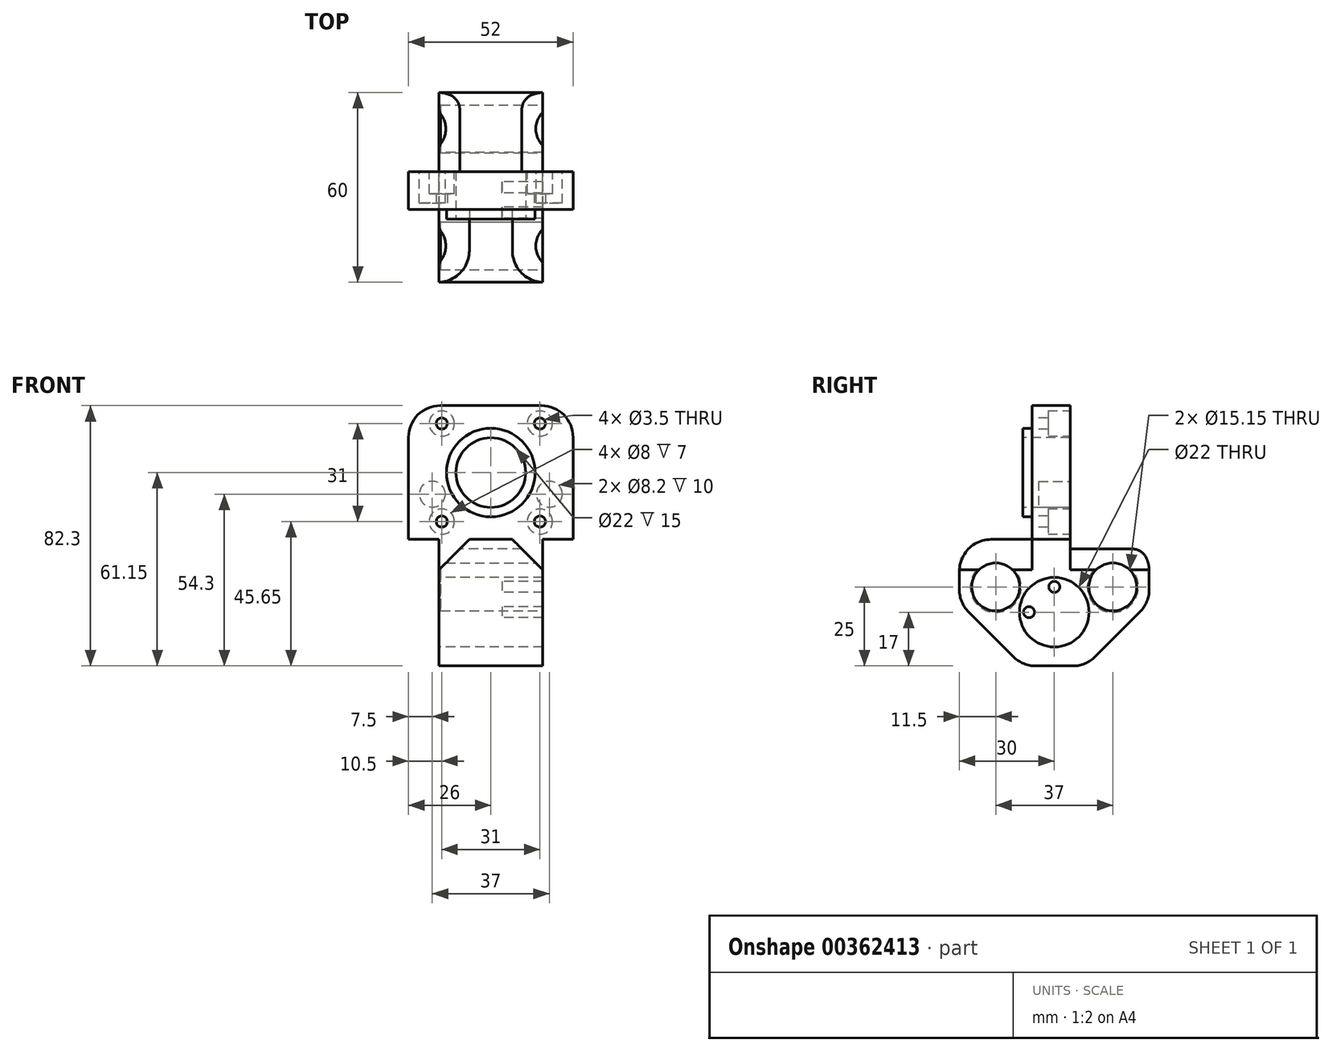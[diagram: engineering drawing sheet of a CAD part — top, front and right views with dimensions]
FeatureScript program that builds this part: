
annotation { "Feature Type Name" : "Feature", "Feature Type Description" : "" }
export const myFeature = defineFeature(function(context is Context, id is Id, definition is map)
    precondition{}
    {
        {
            var Q0;
            Q0=qCreatedBy(makeId("Top.planeOp"),FACE);
            var sketch = newSketch(context, id + "F0", { "sketchPlane" : qUnion([Q0])});
            skLineSegment(sketch, "E0.bottom", {"start": v(16.4, -30) * mm, "end": v(-16.4, -30) * mm});
            skLineSegment(sketch, "E0.top", {"start": v(16.4, 30) * mm, "end": v(-16.4, 30) * mm});
            skLineSegment(sketch, "E0.left", {"start": v(16.4, -30) * mm, "end": v(16.4, 30) * mm});
            skLineSegment(sketch, "E0.right", {"start": v(-16.4, -30) * mm, "end": v(-16.4, 30) * mm});
            skPoint(sketch, "E0.middle", {"position": v(0, 0) * mm});
            skSolve(sketch);
        }
        {
            var Q0;
            Q0=makeQuery(id+"F0.imprint","IMPRINT",FACE,{"disambiguationData":[TD([[makeQuery(id+"F0.imprint","IMPRINT",EDGE,{"derivedFrom":sQuery(id+"F0.wireOp",EDGE,"E0.bottom")}),-1.0]])]});
            extrude(context, id + "F1", {"entities" : qUnion([Q0]), "depth" : 40 * mm});
        }
        {
            var Q0;
            Q0=makeQuery(id+"F1.opExtrude","SWEPT_FACE",FACE,{"disambiguationData":[OSD([sQuery(id+"F0.wireOp",EDGE,"E0.left")])]});
            var sketch = newSketch(context, id + "F2", { "sketchPlane" : qUnion([Q0])});
            skCircle(sketch, "E1", {"center": v(-18.5, 25) * mm, "radius": 7.58 * mm});
            skCircle(sketch, "E2", {"center": v(18.5, 25) * mm, "radius": 7.58 * mm});
            skLineSegment(sketch, "E3", {"start": v(0, 40) * mm, "end": v(0, 0) * mm});
            skCircle(sketch, "E4", {"center": v(0, 17) * mm, "radius": 5.4 * mm});
            skSolve(sketch);
        }
        {
            var Q0;
            Q0=qSketchRegion(id+"F2",true);
            extrude(context, id + "F3", {"entities" : qUnion([Q0]), "operationType" : NewBodyOperationType.REMOVE, "endBound" : BoundingType.THROUGH_ALL, "oppositeDirection" : true, "depth" : 25 * mm});
        }
        {
            var Q0;
            Q0=makeQuery(id+"F1.opExtrude","SWEPT_FACE",FACE,{"disambiguationData":[OSD([sQuery(id+"F0.wireOp",EDGE,"E0.right")])]});
            var sketch = newSketch(context, id + "F4", { "sketchPlane" : qUnion([Q0])});
            skCircle(sketch, "E5", {"center": v(0, 17) * mm, "radius": 11 * mm});
            skSolve(sketch);
        }
        {
            var Q0;
            Q0=makeQuery(id+"F4.imprint","IMPRINT",FACE,{"disambiguationData":[TD([[makeQuery(id+"F4.imprint","IMPRINT",EDGE,{"derivedFrom":sQuery(id+"F4.wireOp",EDGE,"E5")}),1.0]])]});
            extrude(context, id + "F5", {"entities" : qUnion([Q0]), "operationType" : NewBodyOperationType.REMOVE, "oppositeDirection" : true, "depth" : 20 * mm});
        }
        {
            var Q0;
            Q0=makeQuery(id+"F5.boolean.opBoolean","COPY",FACE,{"derivedFrom":makeQuery(id+"F5.opExtrude","CAP_FACE",FACE,{"disambiguationData":[OSD([sQuery(id+"F0.wireOp",EDGE,"E0.right"),sQuery(id+"F2.wireOp",EDGE,"E4"),sQuery(id+"F4.wireOp",EDGE,"E5")])],"isStart":false})});
            var sketch = newSketch(context, id + "F6", { "sketchPlane" : qUnion([Q0])});
            skCircle(sketch, "E6", {"center": v(0, 17) * mm, "radius": 8 * mm});
            skPoint(sketch, "E7", {"position": v(0, 25) * mm});
            skPoint(sketch, "E8", {"position": v(8, 17) * mm});
            skPoint(sketch, "E9", {"position": v(0, 9) * mm});
            skPoint(sketch, "E10", {"position": v(-8, 17) * mm});
            skCircle(sketch, "E11", {"center": v(0, 25) * mm, "radius": 1.75 * mm});
            skCircle(sketch, "E12", {"center": v(8, 17) * mm, "radius": 1.75 * mm});
            skCircle(sketch, "E13", {"center": v(0, 9) * mm, "radius": 1.75 * mm});
            skCircle(sketch, "E14", {"center": v(-8, 17) * mm, "radius": 1.75 * mm});
            skSolve(sketch);
        }
        {
            var Q0;
            {var subQ0=sQuery(id+"F6.wireOp",EDGE,"E11");var subQ1=sQuery(id+"F6.wireOp",EDGE,"E6");var subQ2=makeQuery(id+"F6.imprint","INTERSECT",VERTEX,{"disambiguationData":[OD(0.0)],"derivedFrom":[subQ1,subQ0]});Q0=makeQuery(id+"F6.imprint","IMPRINT",FACE,{"disambiguationData":[TD([[makeQuery(id+"F6.imprint","IMPRINT",EDGE,{"disambiguationData":[TD([[subQ2,-1.0]])],"derivedFrom":subQ1}),1.0]])]});}
            var Q1;
            {var subQ0=sQuery(id+"F6.wireOp",EDGE,"E11");var subQ1=sQuery(id+"F6.wireOp",EDGE,"E6");var subQ2=makeQuery(id+"F6.imprint","INTERSECT",VERTEX,{"disambiguationData":[OD(0.0)],"derivedFrom":[subQ1,subQ0]});Q1=makeQuery(id+"F6.imprint","IMPRINT",FACE,{"disambiguationData":[TD([[makeQuery(id+"F6.imprint","IMPRINT",EDGE,{"disambiguationData":[TD([[subQ2,-1.0]])],"derivedFrom":subQ1}),-1.0]])]});}
            var Q2;
            {var subQ0=sQuery(id+"F6.wireOp",EDGE,"E14");var subQ1=sQuery(id+"F6.wireOp",EDGE,"E6");var subQ2=makeQuery(id+"F6.imprint","INTERSECT",VERTEX,{"disambiguationData":[OD(0.0)],"derivedFrom":[subQ1,subQ0]});Q2=makeQuery(id+"F6.imprint","IMPRINT",FACE,{"disambiguationData":[TD([[makeQuery(id+"F6.imprint","IMPRINT",EDGE,{"disambiguationData":[TD([[subQ2,-1.0]])],"derivedFrom":subQ1}),-1.0]])]});}
            var Q3;
            {var subQ0=sQuery(id+"F6.wireOp",EDGE,"E14");var subQ1=sQuery(id+"F6.wireOp",EDGE,"E6");var subQ2=makeQuery(id+"F6.imprint","INTERSECT",VERTEX,{"disambiguationData":[OD(0.0)],"derivedFrom":[subQ1,subQ0]});Q3=makeQuery(id+"F6.imprint","IMPRINT",FACE,{"disambiguationData":[TD([[makeQuery(id+"F6.imprint","IMPRINT",EDGE,{"disambiguationData":[TD([[subQ2,-1.0]])],"derivedFrom":subQ1}),1.0]])]});}
            var Q4;
            {var subQ0=sQuery(id+"F6.wireOp",EDGE,"E13");var subQ1=sQuery(id+"F6.wireOp",EDGE,"E6");var subQ2=makeQuery(id+"F6.imprint","INTERSECT",VERTEX,{"disambiguationData":[OD(0.0)],"derivedFrom":[subQ1,subQ0]});Q4=makeQuery(id+"F6.imprint","IMPRINT",FACE,{"disambiguationData":[TD([[makeQuery(id+"F6.imprint","IMPRINT",EDGE,{"disambiguationData":[TD([[subQ2,-1.0]])],"derivedFrom":subQ1}),1.0]])]});}
            var Q5;
            {var subQ0=sQuery(id+"F6.wireOp",EDGE,"E13");var subQ1=sQuery(id+"F6.wireOp",EDGE,"E6");var subQ2=makeQuery(id+"F6.imprint","INTERSECT",VERTEX,{"disambiguationData":[OD(0.0)],"derivedFrom":[subQ1,subQ0]});Q5=makeQuery(id+"F6.imprint","IMPRINT",FACE,{"disambiguationData":[TD([[makeQuery(id+"F6.imprint","IMPRINT",EDGE,{"disambiguationData":[TD([[subQ2,-1.0]])],"derivedFrom":subQ1}),-1.0]])]});}
            var Q6;
            {var subQ0=sQuery(id+"F6.wireOp",EDGE,"E12");var subQ1=sQuery(id+"F6.wireOp",EDGE,"E6");var subQ2=makeQuery(id+"F6.imprint","INTERSECT",VERTEX,{"disambiguationData":[OD(0.0)],"derivedFrom":[subQ1,subQ0]});Q6=makeQuery(id+"F6.imprint","IMPRINT",FACE,{"disambiguationData":[TD([[makeQuery(id+"F6.imprint","IMPRINT",EDGE,{"disambiguationData":[TD([[subQ2,1.0]])],"derivedFrom":subQ1}),1.0]])]});}
            var Q7;
            {var subQ0=sQuery(id+"F6.wireOp",EDGE,"E12");var subQ1=sQuery(id+"F6.wireOp",EDGE,"E6");var subQ2=makeQuery(id+"F6.imprint","INTERSECT",VERTEX,{"disambiguationData":[OD(0.0)],"derivedFrom":[subQ1,subQ0]});Q7=makeQuery(id+"F6.imprint","IMPRINT",FACE,{"disambiguationData":[TD([[makeQuery(id+"F6.imprint","IMPRINT",EDGE,{"disambiguationData":[TD([[subQ2,1.0]])],"derivedFrom":subQ1}),-1.0]])]});}
            extrude(context, id + "F7", {"entities" : qUnion([Q0, Q1, Q2, Q3, Q4, Q5, Q6, Q7]), "operationType" : NewBodyOperationType.REMOVE, "endBound" : BoundingType.THROUGH_ALL, "oppositeDirection" : true, "depth" : 25 * mm});
        }
        {
            var Q0;
            Q0=makeQuery(id+"F3.boolean.opBoolean","COPY",EDGE,{"derivedFrom":makeQuery(id+"F3.opExtrude","CAP_EDGE",EDGE,{"disambiguationData":[OSD([sQuery(id+"F2.wireOp",EDGE,"E4")])],"isStart":true})});
            var Q1;
            Q1=makeQuery(id+"F3.boolean.opBoolean","COPY",EDGE,{"derivedFrom":makeQuery(id+"F3.opExtrude","CAP_EDGE",EDGE,{"disambiguationData":[OSD([sQuery(id+"F2.wireOp",EDGE,"E1")])],"isStart":true})});
            var Q2;
            Q2=makeQuery(id+"F3.boolean.opBoolean","COPY",EDGE,{"derivedFrom":makeQuery(id+"F3.opExtrude","CAP_EDGE",EDGE,{"disambiguationData":[OSD([sQuery(id+"F2.wireOp",EDGE,"E2")])],"isStart":true})});
            var Q3;
            Q3=makeQuery(id+"F3.boolean.opBoolean","INTERSECT",EDGE,{"derivedFrom":[makeQuery(id+"F1.opExtrude","SWEPT_FACE",FACE,{"disambiguationData":[OSD([sQuery(id+"F0.wireOp",EDGE,"E0.right")])]}),makeQuery(id+"F3.opExtrude","SWEPT_FACE",FACE,{"disambiguationData":[OSD([sQuery(id+"F2.wireOp",EDGE,"E2")])]})]});
            var Q4;
            Q4=makeQuery(id+"F3.boolean.opBoolean","INTERSECT",EDGE,{"derivedFrom":[makeQuery(id+"F1.opExtrude","SWEPT_FACE",FACE,{"disambiguationData":[OSD([sQuery(id+"F0.wireOp",EDGE,"E0.right")])]}),makeQuery(id+"F3.opExtrude","SWEPT_FACE",FACE,{"disambiguationData":[OSD([sQuery(id+"F2.wireOp",EDGE,"E1")])]})]});
            var Q5;
            Q5=makeQuery(id+"F5.boolean.opBoolean","COPY",EDGE,{"derivedFrom":makeQuery(id+"F5.opExtrude","CAP_EDGE",EDGE,{"disambiguationData":[OSD([sQuery(id+"F4.wireOp",EDGE,"E5")])],"isStart":true})});
            var Q6;
            Q6=makeQuery(id+"F5.boolean.opBoolean","COPY",EDGE,{"derivedFrom":makeQuery(id+"F5.opExtrude","CAP_EDGE",EDGE,{"disambiguationData":[OSD([sQuery(id+"F0.wireOp",EDGE,"E0.right"),sQuery(id+"F2.wireOp",EDGE,"E4")])],"isStart":false})});
            chamfer(context, id + "F8", {"entities" : qUnion([Q0, Q1, Q2, Q3, Q4, Q5, Q6]), "width" : 0.5 * mm, "tangentPropagation" : true});
        }
        {
            var Q0;
            Q0=makeQuery(id+"F1.opExtrude","CAP_EDGE",EDGE,{"disambiguationData":[OSD([sQuery(id+"F0.wireOp",EDGE,"E0.top")])],"isStart":true});
            var Q1;
            Q1=makeQuery(id+"F1.opExtrude","CAP_EDGE",EDGE,{"disambiguationData":[OSD([sQuery(id+"F0.wireOp",EDGE,"E0.bottom")])],"isStart":true});
            chamfer(context, id + "F9", {"entities" : qUnion([Q0, Q1]), "width" : 20 * mm, "tangentPropagation" : true});
        }
        {
            var Q0;
            Q0=makeQuery(id+"F1.opExtrude","CAP_FACE",FACE,{"disambiguationData":[OSD([sQuery(id+"F0.wireOp",EDGE,"E0.bottom"),sQuery(id+"F0.wireOp",EDGE,"E0.top"),sQuery(id+"F0.wireOp",EDGE,"E0.left"),sQuery(id+"F0.wireOp",EDGE,"E0.right")])],"isStart":false});
            var sketch = newSketch(context, id + "F10", { "sketchPlane" : qUnion([Q0])});
            skLineSegment(sketch, "E15.bottom", {"start": v(26, -10) * mm, "end": v(-26, -10) * mm});
            skLineSegment(sketch, "E15.top", {"start": v(26, 10) * mm, "end": v(-26, 10) * mm});
            skLineSegment(sketch, "E15.left", {"start": v(26, -10) * mm, "end": v(26, 10) * mm});
            skLineSegment(sketch, "E15.right", {"start": v(-26, -10) * mm, "end": v(-26, 10) * mm});
            skPoint(sketch, "E15.middle", {"position": v(0, 0) * mm});
            skSolve(sketch);
        }
        {
            var Q0;
            Q0=qSketchRegion(id+"F10",true);
            extrude(context, id + "F11", {"entities" : qUnion([Q0]), "operationType" : NewBodyOperationType.ADD, "depth" : 42.3 * mm});
        }
        {
            var Q0;
            {var subQ0=sQuery(id+"F10.wireOp",EDGE,"E15.top");var subQ1=sQuery(id+"F10.wireOp",EDGE,"E15.bottom");var subQ2=sQuery(id+"F0.wireOp",EDGE,"E0.right");Q0=makeQuery(id+"F11.boolean.opBoolean","SPLIT",EDGE,{"disambiguationData":[TD([makeQuery(id+"F1.opExtrude","CAP_FACE",FACE,{"disambiguationData":[OSD([sQuery(id+"F0.wireOp",EDGE,"E0.bottom"),sQuery(id+"F0.wireOp",EDGE,"E0.top"),sQuery(id+"F0.wireOp",EDGE,"E0.left"),subQ2])],"isStart":false}),makeQuery(id+"F1.opExtrude","SWEPT_FACE",FACE,{"disambiguationData":[OSD([subQ2])]}),makeQuery(id+"F11.opExtrude","SWEPT_FACE",FACE,{"disambiguationData":[OSD([subQ1])]}),makeQuery(id+"F11.opExtrude","CAP_FACE",FACE,{"disambiguationData":[OSD([subQ1,subQ0,sQuery(id+"F10.wireOp",EDGE,"E15.left"),sQuery(id+"F10.wireOp",EDGE,"E15.right")])],"isStart":true}),makeQuery(id+"F11.opExtrude","SWEPT_FACE",FACE,{"disambiguationData":[OSD([subQ0])]})])],"derivedFrom":makeQuery(id+"F1.opExtrude","CAP_EDGE",EDGE,{"disambiguationData":[OSD([subQ2])],"isStart":false})});}
            var Q1;
            {var subQ0=sQuery(id+"F10.wireOp",EDGE,"E15.top");var subQ1=sQuery(id+"F10.wireOp",EDGE,"E15.bottom");var subQ2=sQuery(id+"F0.wireOp",EDGE,"E0.left");Q1=makeQuery(id+"F11.boolean.opBoolean","SPLIT",EDGE,{"disambiguationData":[TD([makeQuery(id+"F1.opExtrude","CAP_FACE",FACE,{"disambiguationData":[OSD([sQuery(id+"F0.wireOp",EDGE,"E0.bottom"),sQuery(id+"F0.wireOp",EDGE,"E0.top"),subQ2,sQuery(id+"F0.wireOp",EDGE,"E0.right")])],"isStart":false}),makeQuery(id+"F1.opExtrude","SWEPT_FACE",FACE,{"disambiguationData":[OSD([subQ2])]}),makeQuery(id+"F11.opExtrude","SWEPT_FACE",FACE,{"disambiguationData":[OSD([subQ1])]}),makeQuery(id+"F11.opExtrude","CAP_FACE",FACE,{"disambiguationData":[OSD([subQ1,subQ0,sQuery(id+"F10.wireOp",EDGE,"E15.left"),sQuery(id+"F10.wireOp",EDGE,"E15.right")])],"isStart":true}),makeQuery(id+"F11.opExtrude","SWEPT_FACE",FACE,{"disambiguationData":[OSD([subQ0])]})])],"derivedFrom":makeQuery(id+"F1.opExtrude","CAP_EDGE",EDGE,{"disambiguationData":[OSD([subQ2])],"isStart":false})});}
            chamfer(context, id + "F12", {"entities" : qUnion([Q0, Q1]), "width" : 9.6 * mm, "tangentPropagation" : true});
        }
        {
            var Q0;
            Q0=makeQuery(id+"F11.opExtrude","SWEPT_FACE",FACE,{"disambiguationData":[OSD([sQuery(id+"F10.wireOp",EDGE,"E15.bottom")])]});
            var sketch = newSketch(context, id + "F13", { "sketchPlane" : qUnion([Q0])});
            skLineSegment(sketch, "E16", {"start": v(-26, 82.3) * mm, "end": v(26, 40) * mm});
            skCircle(sketch, "E17", {"center": v(0, 61.15) * mm, "radius": 14 * mm});
            skSolve(sketch);
        }
        {
            var Q0;
            {var subQ0=sQuery(id+"F13.wireOp",EDGE,"E17");var subQ1=sQuery(id+"F13.wireOp",EDGE,"E16");var subQ2=makeQuery(id+"F13.imprint","INTERSECT",VERTEX,{"disambiguationData":[OD(0.0)],"derivedFrom":[subQ1,subQ0]});Q0=makeQuery(id+"F13.imprint","IMPRINT",FACE,{"disambiguationData":[TD([[makeQuery(id+"F13.imprint","IMPRINT",EDGE,{"disambiguationData":[TD([[subQ2,-1.0]])],"derivedFrom":subQ1}),1.0]])]});}
            var Q1;
            {var subQ0=sQuery(id+"F13.wireOp",EDGE,"E17");var subQ1=sQuery(id+"F13.wireOp",EDGE,"E16");var subQ2=makeQuery(id+"F13.imprint","INTERSECT",VERTEX,{"disambiguationData":[OD(0.0)],"derivedFrom":[subQ1,subQ0]});Q1=makeQuery(id+"F13.imprint","IMPRINT",FACE,{"disambiguationData":[TD([[makeQuery(id+"F13.imprint","IMPRINT",EDGE,{"disambiguationData":[TD([[subQ2,-1.0]])],"derivedFrom":subQ1}),-1.0]])]});}
            extrude(context, id + "F14", {"entities" : qUnion([Q0, Q1]), "operationType" : NewBodyOperationType.REMOVE, "oppositeDirection" : true, "depth" : 3 * mm});
        }
        {
            var Q0;
            Q0=makeQuery(id+"F11.opExtrude","SWEPT_FACE",FACE,{"disambiguationData":[OSD([sQuery(id+"F10.wireOp",EDGE,"E15.bottom")])]});
            var sketch = newSketch(context, id + "F15", { "sketchPlane" : qUnion([Q0])});
            skCircle(sketch, "E18", {"center": v(0, 61.15) * mm, "radius": 11 * mm});
            skCircle(sketch, "E19", {"center": v(-15.5, 76.65) * mm, "radius": 1.75 * mm});
            skCircle(sketch, "E20.0.1.0", {"center": v(-15.5, 45.65) * mm, "radius": 1.75 * mm});
            skCircle(sketch, "E20.1.0.0", {"center": v(15.5, 76.65) * mm, "radius": 1.75 * mm});
            skCircle(sketch, "E20.1.1.0", {"center": v(15.5, 45.65) * mm, "radius": 1.75 * mm});
            skLineSegment(sketch, "E20.direction1", {"start": v(-15.5, 76.65) * mm, "end": v(15.5, 76.65) * mm, "construction": true});
            skLineSegment(sketch, "E20.direction2", {"start": v(-15.5, 76.65) * mm, "end": v(-15.5, 45.65) * mm, "construction": true});
            skSolve(sketch);
        }
        {
            var Q0;
            Q0=makeQuery(id+"F15.imprint","IMPRINT",FACE,{"disambiguationData":[TD([[makeQuery(id+"F15.imprint","IMPRINT",EDGE,{"derivedFrom":sQuery(id+"F15.wireOp",EDGE,"E19")}),1.0]])]});
            var Q1;
            Q1=makeQuery(id+"F15.imprint","IMPRINT",FACE,{"disambiguationData":[TD([[makeQuery(id+"F15.imprint","IMPRINT",EDGE,{"derivedFrom":sQuery(id+"F15.wireOp",EDGE,"E20.0.1.0")}),1.0]])]});
            var Q2;
            Q2=makeQuery(id+"F15.imprint","IMPRINT",FACE,{"disambiguationData":[TD([[makeQuery(id+"F15.imprint","IMPRINT",EDGE,{"derivedFrom":sQuery(id+"F15.wireOp",EDGE,"E20.1.1.0")}),1.0]])]});
            var Q3;
            Q3=makeQuery(id+"F15.imprint","IMPRINT",FACE,{"disambiguationData":[TD([[makeQuery(id+"F15.imprint","IMPRINT",EDGE,{"derivedFrom":sQuery(id+"F15.wireOp",EDGE,"E20.1.0.0")}),1.0]])]});
            var Q4;
            Q4=makeQuery(id+"F15.imprint","IMPRINT",FACE,{"disambiguationData":[TD([[makeQuery(id+"F15.imprint","IMPRINT",EDGE,{"derivedFrom":sQuery(id+"F15.wireOp",EDGE,"E18")}),1.0]])]});
            extrude(context, id + "F16", {"entities" : qUnion([Q0, Q1, Q2, Q3, Q4]), "operationType" : NewBodyOperationType.REMOVE, "endBound" : BoundingType.THROUGH_ALL, "oppositeDirection" : true, "depth" : 25 * mm});
        }
        {
            var Q0;
            Q0=makeQuery(id+"F11.opExtrude","SWEPT_FACE",FACE,{"disambiguationData":[OSD([sQuery(id+"F10.wireOp",EDGE,"E15.top")])]});
            var sketch = newSketch(context, id + "F17", { "sketchPlane" : qUnion([Q0])});
            skCircle(sketch, "E21", {"center": v(-15.5, 76.65) * mm, "radius": 4 * mm});
            skCircle(sketch, "E22", {"center": v(15.5, 76.65) * mm, "radius": 4 * mm});
            skCircle(sketch, "E23", {"center": v(15.5, 45.65) * mm, "radius": 4 * mm});
            skCircle(sketch, "E24", {"center": v(-15.5, 45.65) * mm, "radius": 4 * mm});
            skSolve(sketch);
        }
        {
            var Q0;
            Q0=qSketchRegion(id+"F17",true);
            extrude(context, id + "F18", {"entities" : qUnion([Q0]), "operationType" : NewBodyOperationType.REMOVE, "oppositeDirection" : true, "depth" : 12 * mm});
        }
        {
            var Q0;
            Q0=makeQuery(id+"F11.opExtrude","SWEPT_FACE",FACE,{"disambiguationData":[OSD([sQuery(id+"F10.wireOp",EDGE,"E15.top")])]});
            var sketch = newSketch(context, id + "F19", { "sketchPlane" : qUnion([Q0])});
            skCircle(sketch, "E25", {"center": v(-18.5, 54.3) * mm, "radius": 4.1 * mm});
            skLineSegment(sketch, "E26", {"start": v(0, 82.3) * mm, "end": v(0, 40) * mm});
            skCircle(sketch, "E27.MirrorC", {"center": v(18.5, 54.3) * mm, "radius": 4.1 * mm});
            skSolve(sketch);
        }
        {
            var Q0;
            Q0=qSketchRegion(id+"F19",true);
            extrude(context, id + "F20", {"entities" : qUnion([Q0]), "operationType" : NewBodyOperationType.REMOVE, "oppositeDirection" : true, "depth" : 15 * mm});
        }
        {
            var Q0;
            Q0=makeQuery(id+"F11.opExtrude","CAP_EDGE",EDGE,{"disambiguationData":[OSD([sQuery(id+"F10.wireOp",EDGE,"E15.left")])],"isStart":false});
            var Q1;
            {var subQ0=sQuery(id+"F10.wireOp",EDGE,"E15.left");var subQ1=sQuery(id+"F10.wireOp",EDGE,"E15.top");var subQ2=sQuery(id+"F10.wireOp",EDGE,"E15.bottom");var subQ3=sQuery(id+"F0.wireOp",EDGE,"E0.left");Q1=makeQuery(id+"F12.opChamfer","BLEND_EDGE",EDGE,{"blendedFrom":[makeQuery(id+"F11.boolean.opBoolean","SPLIT",EDGE,{"disambiguationData":[TD([makeQuery(id+"F1.opExtrude","CAP_FACE",FACE,{"disambiguationData":[OSD([sQuery(id+"F0.wireOp",EDGE,"E0.bottom"),sQuery(id+"F0.wireOp",EDGE,"E0.top"),subQ3,sQuery(id+"F0.wireOp",EDGE,"E0.right")])],"isStart":false}),makeQuery(id+"F1.opExtrude","SWEPT_FACE",FACE,{"disambiguationData":[OSD([subQ3])]}),makeQuery(id+"F11.opExtrude","SWEPT_FACE",FACE,{"disambiguationData":[OSD([subQ2])]}),makeQuery(id+"F11.opExtrude","CAP_FACE",FACE,{"disambiguationData":[OSD([subQ2,subQ1,subQ0,sQuery(id+"F10.wireOp",EDGE,"E15.right")])],"isStart":true}),makeQuery(id+"F11.opExtrude","SWEPT_FACE",FACE,{"disambiguationData":[OSD([subQ1])]})])],"derivedFrom":makeQuery(id+"F1.opExtrude","CAP_EDGE",EDGE,{"disambiguationData":[OSD([subQ3])],"isStart":false})}),makeQuery(id+"F11.opExtrude","SWEPT_FACE",FACE,{"disambiguationData":[OSD([subQ0])]})],"blendedInto":[makeQuery(id+"F11.opExtrude","SWEPT_FACE",FACE,{"disambiguationData":[OSD([subQ0])]})]});}
            var Q2;
            Q2=makeQuery(id+"F11.opExtrude","CAP_EDGE",EDGE,{"disambiguationData":[OSD([sQuery(id+"F10.wireOp",EDGE,"E15.right")])],"isStart":false});
            var Q3;
            {var subQ0=sQuery(id+"F10.wireOp",EDGE,"E15.right");var subQ1=sQuery(id+"F10.wireOp",EDGE,"E15.top");var subQ2=sQuery(id+"F10.wireOp",EDGE,"E15.bottom");var subQ3=sQuery(id+"F0.wireOp",EDGE,"E0.right");Q3=makeQuery(id+"F12.opChamfer","BLEND_EDGE",EDGE,{"blendedFrom":[makeQuery(id+"F11.boolean.opBoolean","SPLIT",EDGE,{"disambiguationData":[TD([makeQuery(id+"F1.opExtrude","CAP_FACE",FACE,{"disambiguationData":[OSD([sQuery(id+"F0.wireOp",EDGE,"E0.bottom"),sQuery(id+"F0.wireOp",EDGE,"E0.top"),sQuery(id+"F0.wireOp",EDGE,"E0.left"),subQ3])],"isStart":false}),makeQuery(id+"F1.opExtrude","SWEPT_FACE",FACE,{"disambiguationData":[OSD([subQ3])]}),makeQuery(id+"F11.opExtrude","SWEPT_FACE",FACE,{"disambiguationData":[OSD([subQ2])]}),makeQuery(id+"F11.opExtrude","CAP_FACE",FACE,{"disambiguationData":[OSD([subQ2,subQ1,sQuery(id+"F10.wireOp",EDGE,"E15.left"),subQ0])],"isStart":true}),makeQuery(id+"F11.opExtrude","SWEPT_FACE",FACE,{"disambiguationData":[OSD([subQ1])]})])],"derivedFrom":makeQuery(id+"F1.opExtrude","CAP_EDGE",EDGE,{"disambiguationData":[OSD([subQ3])],"isStart":false})}),makeQuery(id+"F11.opExtrude","SWEPT_FACE",FACE,{"disambiguationData":[OSD([subQ0])]})],"blendedInto":[makeQuery(id+"F11.opExtrude","SWEPT_FACE",FACE,{"disambiguationData":[OSD([subQ0])]})]});}
            var Q4;
            Q4=makeQuery(id+"F1.opExtrude","CAP_EDGE",EDGE,{"disambiguationData":[OSD([sQuery(id+"F0.wireOp",EDGE,"E0.top")])],"isStart":false});
            var Q5;
            Q5=makeQuery(id+"F1.opExtrude","CAP_EDGE",EDGE,{"disambiguationData":[OSD([sQuery(id+"F0.wireOp",EDGE,"E0.bottom")])],"isStart":false});
            var Q6;
            {var subQ0=sQuery(id+"F0.wireOp",EDGE,"E0.bottom");Q6=makeQuery(id+"F9.opChamfer","BLEND_EDGE",EDGE,{"blendedFrom":[makeQuery(id+"F1.opExtrude","CAP_EDGE",EDGE,{"disambiguationData":[OSD([subQ0])],"isStart":true}),makeQuery(id+"F1.opExtrude","SWEPT_FACE",FACE,{"disambiguationData":[OSD([subQ0])]})],"blendedInto":[makeQuery(id+"F1.opExtrude","SWEPT_FACE",FACE,{"disambiguationData":[OSD([subQ0])]})]});}
            var Q7;
            {var subQ0=sQuery(id+"F0.wireOp",EDGE,"E0.top");Q7=makeQuery(id+"F9.opChamfer","BLEND_EDGE",EDGE,{"blendedFrom":[makeQuery(id+"F1.opExtrude","CAP_EDGE",EDGE,{"disambiguationData":[OSD([subQ0])],"isStart":true}),makeQuery(id+"F1.opExtrude","SWEPT_FACE",FACE,{"disambiguationData":[OSD([subQ0])]})],"blendedInto":[makeQuery(id+"F1.opExtrude","SWEPT_FACE",FACE,{"disambiguationData":[OSD([subQ0])]})]});}
            var Q8;
            {var subQ0=sQuery(id+"F0.wireOp",EDGE,"E0.top");Q8=makeQuery(id+"F9.opChamfer","BLEND_EDGE",EDGE,{"blendedFrom":[makeQuery(id+"F1.opExtrude","CAP_EDGE",EDGE,{"disambiguationData":[OSD([subQ0])],"isStart":true}),makeQuery(id+"F1.opExtrude","CAP_FACE",FACE,{"disambiguationData":[OSD([sQuery(id+"F0.wireOp",EDGE,"E0.bottom"),subQ0,sQuery(id+"F0.wireOp",EDGE,"E0.left"),sQuery(id+"F0.wireOp",EDGE,"E0.right")])],"isStart":true})],"blendedInto":[makeQuery(id+"F1.opExtrude","CAP_FACE",FACE,{"disambiguationData":[OSD([sQuery(id+"F0.wireOp",EDGE,"E0.bottom"),subQ0,sQuery(id+"F0.wireOp",EDGE,"E0.left"),sQuery(id+"F0.wireOp",EDGE,"E0.right")])],"isStart":true})]});}
            var Q9;
            {var subQ0=sQuery(id+"F0.wireOp",EDGE,"E0.bottom");Q9=makeQuery(id+"F9.opChamfer","BLEND_EDGE",EDGE,{"blendedFrom":[makeQuery(id+"F1.opExtrude","CAP_EDGE",EDGE,{"disambiguationData":[OSD([subQ0])],"isStart":true}),makeQuery(id+"F1.opExtrude","CAP_FACE",FACE,{"disambiguationData":[OSD([subQ0,sQuery(id+"F0.wireOp",EDGE,"E0.top"),sQuery(id+"F0.wireOp",EDGE,"E0.left"),sQuery(id+"F0.wireOp",EDGE,"E0.right")])],"isStart":true})],"blendedInto":[makeQuery(id+"F1.opExtrude","CAP_FACE",FACE,{"disambiguationData":[OSD([subQ0,sQuery(id+"F0.wireOp",EDGE,"E0.top"),sQuery(id+"F0.wireOp",EDGE,"E0.left"),sQuery(id+"F0.wireOp",EDGE,"E0.right")])],"isStart":true})]});}
            fillet(context, id + "F21", {"entities" : qUnion([Q0, Q1, Q2, Q3, Q4, Q5, Q6, Q7, Q8, Q9]), "radius" : 10 * mm, "tangentPropagation" : true, "allowEdgeOverflow" : false});
        }
        {
            var Q0;
            Q0=makeQuery(id+"F11.opExtrude","SWEPT_FACE",FACE,{"disambiguationData":[OSD([sQuery(id+"F10.wireOp",EDGE,"E15.top")])]});
            extrude(context, id + "F22", {"entities" : qUnion([Q0]), "operationType" : NewBodyOperationType.REMOVE, "oppositeDirection" : true, "depth" : 5 * mm});
        }
        {
            var Q0;
            Q0=makeQuery(id+"F22.boolean.opBoolean","COPY",FACE,{"derivedFrom":makeQuery(id+"F22.opExtrude","CAP_FACE",FACE,{"disambiguationData":[OSD([sQuery(id+"F10.wireOp",EDGE,"E15.top")])],"isStart":false})});
            var sketch = newSketch(context, id + "F23", { "sketchPlane" : qUnion([Q0])});
            skLineSegment(sketch, "E28.bottom", {"start": v(-10, 40) * mm, "end": v(10, 40) * mm});
            skLineSegment(sketch, "E28.top", {"start": v(-10, 37) * mm, "end": v(10, 37) * mm});
            skLineSegment(sketch, "E28.left", {"start": v(-10, 40) * mm, "end": v(-10, 37) * mm});
            skLineSegment(sketch, "E28.right", {"start": v(10, 40) * mm, "end": v(10, 37) * mm});
            skSolve(sketch);
        }
        {
            var Q0;
            Q0=qSketchRegion(id+"F23",true);
            extrude(context, id + "F24", {"entities" : qUnion([Q0]), "operationType" : NewBodyOperationType.REMOVE, "endBound" : BoundingType.THROUGH_ALL, "depth" : 25 * mm});
        }
        {
            var Q0;
            {var subQ0=sQuery(id+"F0.wireOp",EDGE,"E0.top");Q0=makeQuery(id+"F24.boolean.opBoolean","INTERSECT",EDGE,{"derivedFrom":[makeQuery(id+"F21.opFillet","BLEND_FACE",FACE,{"disambiguationData":[OSD([subQ0]),TDD([makeQuery(id+"F1.opExtrude","CAP_EDGE",EDGE,{"disambiguationData":[OSD([subQ0])],"isStart":false})])]}),makeQuery(id+"F24.opExtrude","SWEPT_FACE",FACE,{"disambiguationData":[OSD([sQuery(id+"F23.wireOp",EDGE,"E28.top")])]})]});}
            fillet(context, id + "F25", {"entities" : qUnion([Q0]), "radius" : 5 * mm, "tangentPropagation" : true, "allowEdgeOverflow" : false});
        }
    });
